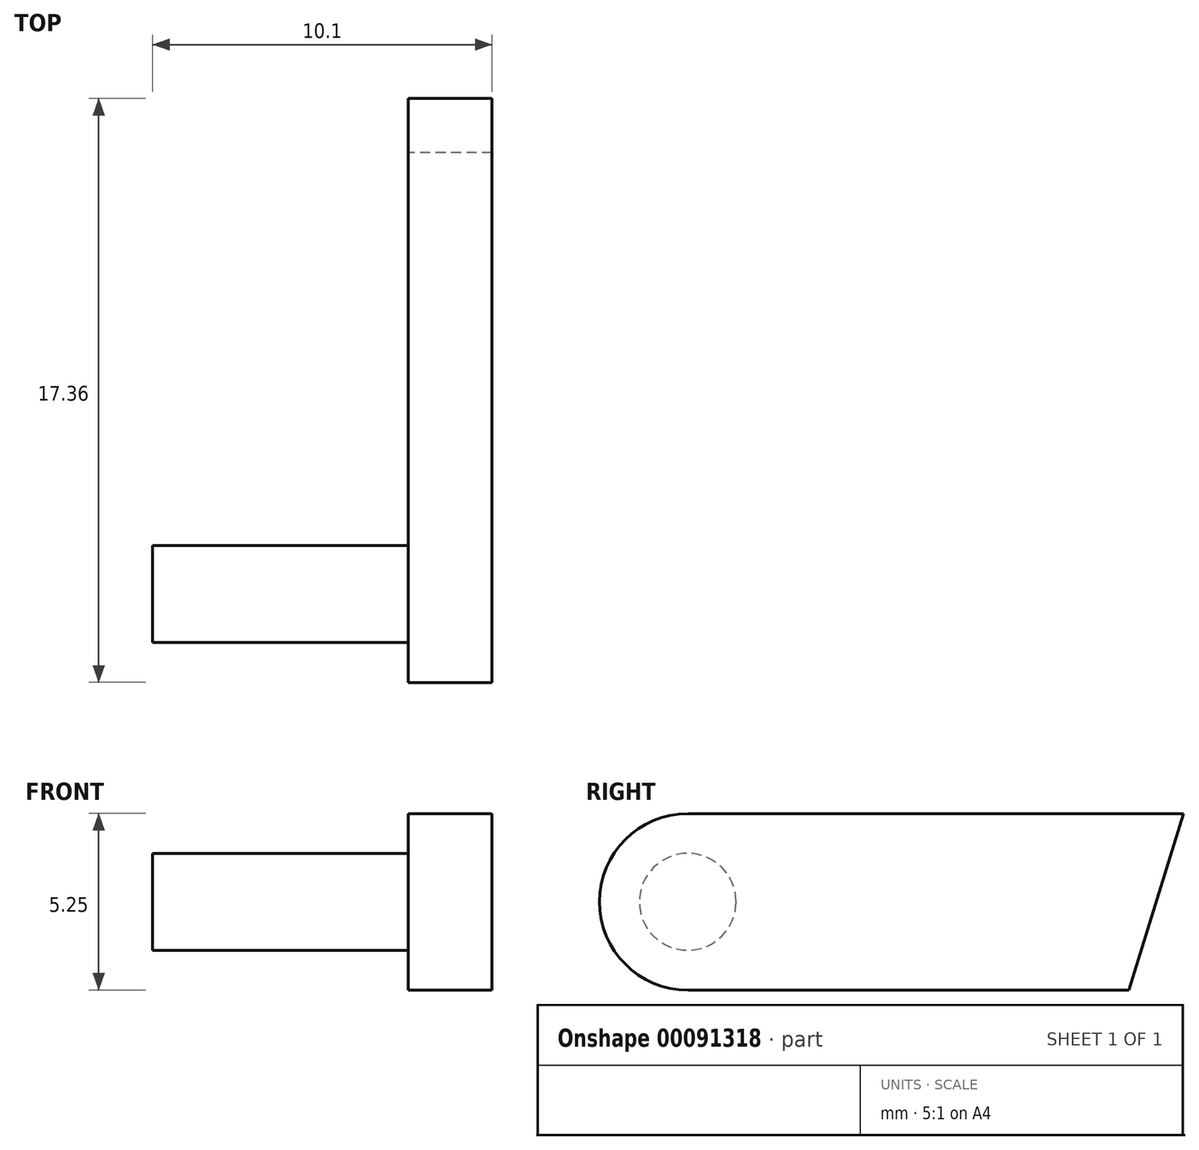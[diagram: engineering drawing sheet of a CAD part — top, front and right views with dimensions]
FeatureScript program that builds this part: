
annotation { "Feature Type Name" : "Feature", "Feature Type Description" : "" }
export const myFeature = defineFeature(function(context is Context, id is Id, definition is map)
    precondition{}
    {
        {
            var Q0;
            Q0=qCreatedBy(makeId("Right.planeOp"),FACE);
            var sketch = newSketch(context, id + "F0", { "sketchPlane" : qUnion([Q0])});
            skCircle(sketch, "E0", {"center": v(0, 0) * mm, "radius": 2.62 * mm});
            skLineSegment(sketch, "E1", {"start": v(0, -2.62) * mm, "end": v(13.12, -2.62) * mm});
            skLineSegment(sketch, "E2", {"start": v(-2.63, 0) * mm, "end": v(-2.63, -2.62) * mm, "construction": true});
            skLineSegment(sketch, "E3", {"start": v(-2.63, -2.62) * mm, "end": v(0, -2.62) * mm, "construction": true});
            skLineSegment(sketch, "E4", {"start": v(0, 2.62) * mm, "end": v(14.74, 2.62) * mm});
            skLineSegment(sketch, "E5", {"start": v(13.12, -2.62) * mm, "end": v(14.74, 2.62) * mm});
            skSolve(sketch);
        }
        {
            var Q0;
            Q0 = qSketchRegion(id + "F0", true);
            extrude(context, id + "F1", {"entities" : qUnion([Q0]), "depth" : 2.5 * mm});
        }
        {
            var Q0;
            Q0=makeQuery(id+"F1.opExtrude","CAP_FACE",FACE,{"disambiguationData":[OSD([sQuery(id+"F0.wireOp",EDGE,"E0"),sQuery(id+"F0.wireOp",EDGE,"E1"),sQuery(id+"F0.wireOp",EDGE,"E4"),sQuery(id+"F0.wireOp",EDGE,"E5")])],"isStart":true});
            var sketch = newSketch(context, id + "F2", { "sketchPlane" : qUnion([Q0])});
            skCircle(sketch, "E6", {"center": v(0, 0) * mm, "radius": 1.44 * mm});
            skSolve(sketch);
        }
        {
            var Q0;
            Q0 = qSketchRegion(id + "F2", true);
            extrude(context, id + "F3", {"entities" : qUnion([Q0]), "operationType" : NewBodyOperationType.ADD, "depth" : 15.2 * mm / 2});
        }
    });
